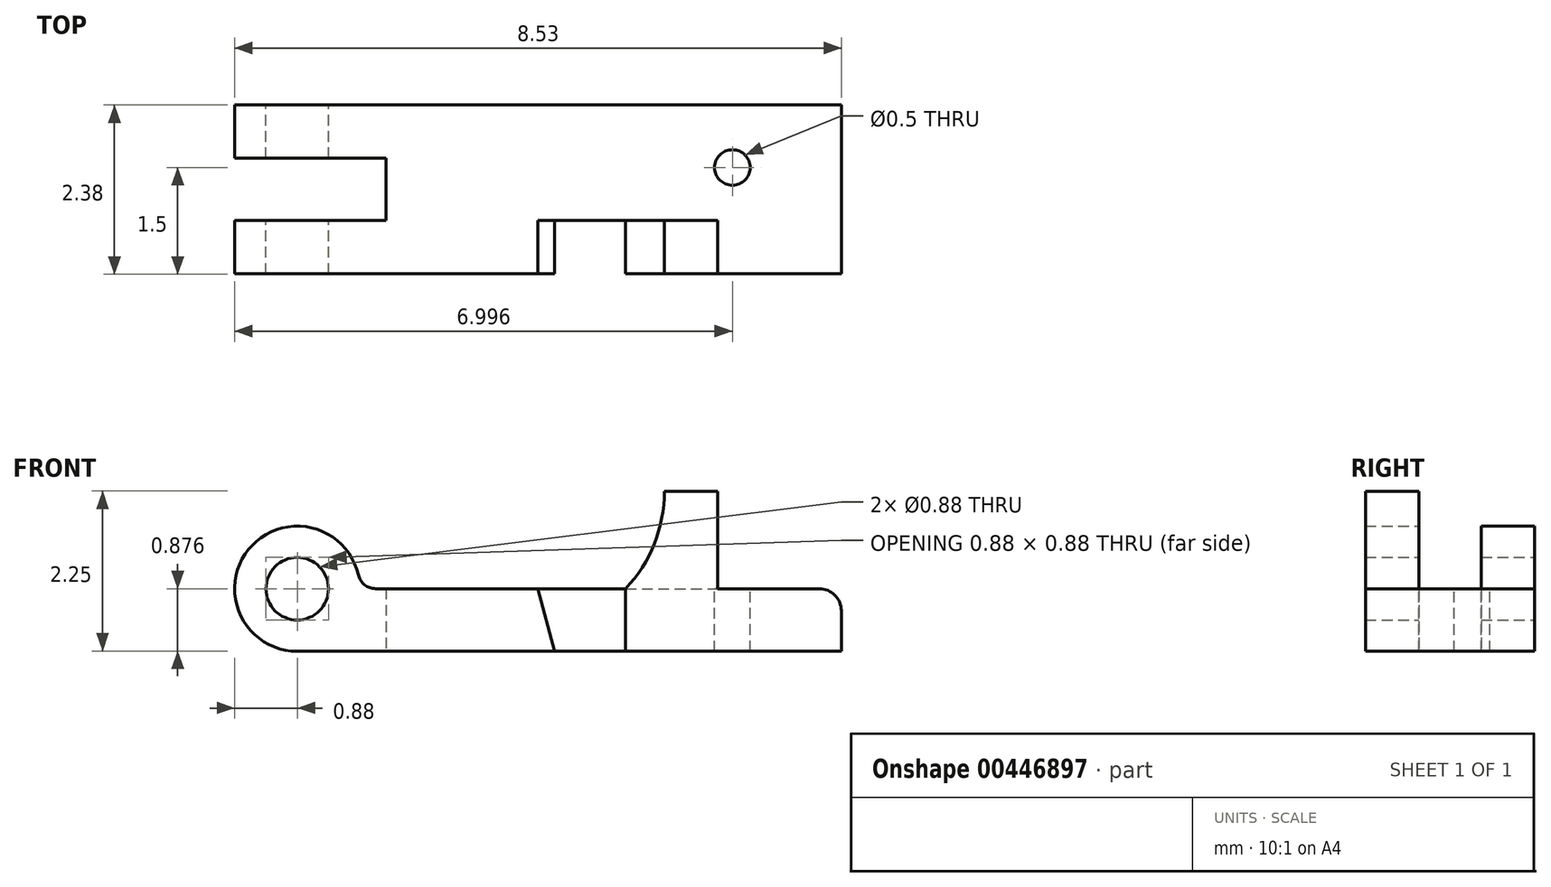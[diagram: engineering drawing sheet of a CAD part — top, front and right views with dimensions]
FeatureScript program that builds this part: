
annotation { "Feature Type Name" : "Feature", "Feature Type Description" : "" }
export const myFeature = defineFeature(function(context is Context, id is Id, definition is map)
    precondition{}
    {
        {
            var Q0;
            Q0=qCreatedBy(makeId("Front.planeOp"),FACE);
            var sketch = newSketch(context, id + "F0", { "sketchPlane" : qUnion([Q0])});
            skArc(sketch, "E0", {"start": v(-5.16, 10.86) * mm, "mid": v(-6.7, 11.22) * mm, "end": v(-6.02, 9.79) * mm});
            skLineSegment(sketch, "E1.bottom", {"start": v(-4.92, 10.67) * mm, "end": v(1.63, 10.67) * mm});
            skLineSegment(sketch, "E1.top", {"start": v(-5.56, 9.79) * mm, "end": v(1.63, 9.79) * mm});
            skLineSegment(sketch, "E1.right", {"start": v(1.63, 10.67) * mm, "end": v(1.63, 9.79) * mm});
            skLineSegment(sketch, "E2", {"start": v(-5.56, 9.79) * mm, "end": v(-6.02, 9.79) * mm});
            skPoint(sketch, "E3.visualSharp", {"position": v(-5.14, 10.67) * mm});
            skArc(sketch, "E3.filletArc", {"start": v(-5.16, 10.86) * mm, "mid": v(-5.07, 10.72) * mm, "end": v(-4.92, 10.67) * mm});
            skCircle(sketch, "E4", {"center": v(-6.02, 10.67) * mm, "radius": 0.44 * mm});
            skSolve(sketch);
        }
        {
            var Q0;
            Q0=makeQuery(id+"F0.imprint","IMPRINT",FACE,{"disambiguationData":[TD([[makeQuery(id+"F0.imprint","IMPRINT",EDGE,{"derivedFrom":sQuery(id+"F0.wireOp",EDGE,"E0")}),1.0]])]});
            extrude(context, id + "F1", {"entities" : qUnion([Q0]), "depth" : 2.38 * mm});
        }
        {
            var Q0;
            Q0=qCreatedBy(makeId("Top.planeOp"),FACE);
            var sketch = newSketch(context, id + "F2", { "sketchPlane" : qUnion([Q0])});
            skLineSegment(sketch, "E5.bottom", {"start": v(-7.37, -0.75) * mm, "end": v(-4.77, -0.75) * mm});
            skLineSegment(sketch, "E5.top", {"start": v(-7.37, -1.63) * mm, "end": v(-4.77, -1.63) * mm});
            skLineSegment(sketch, "E5.left", {"start": v(-7.37, -0.75) * mm, "end": v(-7.37, -1.63) * mm});
            skLineSegment(sketch, "E5.right", {"start": v(-4.77, -0.75) * mm, "end": v(-4.77, -1.63) * mm});
            skSolve(sketch);
        }
        {
            var Q0;
            Q0=makeQuery(id+"F2.imprint","IMPRINT",FACE,{"disambiguationData":[TD([[makeQuery(id+"F2.imprint","IMPRINT",EDGE,{"derivedFrom":sQuery(id+"F2.wireOp",EDGE,"E5.bottom")}),-1.0]])]});
            extrude(context, id + "F3", {"entities" : qUnion([Q0]), "operationType" : NewBodyOperationType.REMOVE, "depth" : 25 * mm});
        }
        {
            var Q0;
            Q0=makeQuery(id+"F1.opExtrude","CAP_FACE",FACE,{"disambiguationData":[OSD([sQuery(id+"F0.wireOp",EDGE,"E0"),sQuery(id+"F0.wireOp",EDGE,"E1.bottom"),sQuery(id+"F0.wireOp",EDGE,"E1.top"),sQuery(id+"F0.wireOp",EDGE,"E1.right"),sQuery(id+"F0.wireOp",EDGE,"E2"),sQuery(id+"F0.wireOp",EDGE,"E3.filletArc"),sQuery(id+"F0.wireOp",EDGE,"E4")])],"isStart":false});
            var sketch = newSketch(context, id + "F4", { "sketchPlane" : qUnion([Q0])});
            skLineSegment(sketch, "E6", {"start": v(-2.64, 10.67) * mm, "end": v(-2.4, 9.79) * mm});
            skLineSegment(sketch, "E7", {"start": v(-1.4, 10.67) * mm, "end": v(-1.4, 9.79) * mm});
            skLineSegment(sketch, "E8.0", {"start": v(-4.92, 10.67) * mm, "end": v(1.63, 10.67) * mm});
            skLineSegment(sketch, "E9.0", {"start": v(1.63, 9.79) * mm, "end": v(-6.02, 9.79) * mm});
            skLineSegment(sketch, "E10.0.0", {"start": v(1.63, 9.79) * mm, "end": v(1.63, 10.67) * mm});
            skLineSegment(sketch, "E10.0.1", {"start": v(1.63, 10.67) * mm, "end": v(-4.92, 10.67) * mm});
            skArc(sketch, "E10.0.2", {"start": v(-4.92, 10.67) * mm, "mid": v(-5.07, 10.72) * mm, "end": v(-5.16, 10.86) * mm});
            skArc(sketch, "E10.0.3", {"start": v(-5.16, 10.86) * mm, "mid": v(-6.7, 11.22) * mm, "end": v(-6.02, 9.79) * mm});
            skLineSegment(sketch, "E10.0.4", {"start": v(-6.02, 9.79) * mm, "end": v(1.63, 9.79) * mm});
            skSolve(sketch);
        }
        {
            var Q0;
            {var subQ0=sQuery(id+"F4.wireOp",EDGE,"E6");Q0=makeQuery(id+"F4.imprint","IMPRINT",FACE,{"disambiguationData":[TD([[makeQuery(id+"F4.imprint","IMPRINT",EDGE,{"derivedFrom":subQ0}),1.0]])]});}
            extrude(context, id + "F5", {"entities" : qUnion([Q0]), "operationType" : NewBodyOperationType.REMOVE, "oppositeDirection" : true, "depth" : 0.75 * mm});
        }
        {
            var Q0;
            {var subQ0=sQuery(id+"F0.wireOp",EDGE,"E1.bottom");var subQ1=sQuery(id+"F0.wireOp",EDGE,"E2");var subQ2=sQuery(id+"F0.wireOp",EDGE,"E1.top");var subQ3=sQuery(id+"F0.wireOp",EDGE,"E1.right");Q0=makeQuery(id+"F5.boolean.opBoolean","SPLIT",FACE,{"disambiguationData":[TD([makeQuery(id+"F1.opExtrude","SWEPT_FACE",FACE,{"disambiguationData":[OSD([subQ3])]})])],"derivedFrom":makeQuery(id+"F1.opExtrude","CAP_FACE",FACE,{"disambiguationData":[OSD([sQuery(id+"F0.wireOp",EDGE,"E0"),subQ0,subQ2,subQ3,subQ1,sQuery(id+"F0.wireOp",EDGE,"E3.filletArc"),sQuery(id+"F0.wireOp",EDGE,"E4")])],"isStart":false})});}
            var sketch = newSketch(context, id + "F6", { "sketchPlane" : qUnion([Q0])});
            skLineSegment(sketch, "E11.0", {"start": v(-1.4, 10.67) * mm, "end": v(-1.4, 9.79) * mm});
            skLineSegment(sketch, "E12", {"start": v(-0.11, 10.67) * mm, "end": v(-0.11, 12.04) * mm});
            skLineSegment(sketch, "E13", {"start": v(-0.11, 12.04) * mm, "end": v(-0.86, 12.04) * mm});
            skArc(sketch, "E14", {"start": v(-1.4, 10.67) * mm, "mid": v(-1, 11.3) * mm, "end": v(-0.86, 12.04) * mm});
            skSolve(sketch);
        }
        {
            var Q0;
            {var subQ0=sQuery(id+"F6.wireOp",EDGE,"E12");Q0=makeQuery(id+"F6.imprint","IMPRINT",FACE,{"disambiguationData":[TD([[makeQuery(id+"F6.imprint","IMPRINT",EDGE,{"derivedFrom":subQ0}),1.0]])]});}
            extrude(context, id + "F7", {"entities" : qUnion([Q0]), "operationType" : NewBodyOperationType.ADD, "oppositeDirection" : true, "depth" : 0.75 * mm});
        }
        {
            var Q0;
            Q0=makeQuery(id+"F1.opExtrude","SWEPT_FACE",FACE,{"disambiguationData":[OSD([sQuery(id+"F0.wireOp",EDGE,"E1.bottom")])]});
            var sketch = newSketch(context, id + "F8", { "sketchPlane" : qUnion([Q0])});
            skCircle(sketch, "E15", {"center": v(0.1, -0.88) * mm, "radius": 0.25 * mm});
            skSolve(sketch);
        }
        {
            var Q0;
            Q0=makeQuery(id+"F8.imprint","IMPRINT",FACE,{"disambiguationData":[TD([[makeQuery(id+"F8.imprint","IMPRINT",EDGE,{"derivedFrom":sQuery(id+"F8.wireOp",EDGE,"E15")}),1.0]])]});
            extrude(context, id + "F9", {"entities" : qUnion([Q0]), "operationType" : NewBodyOperationType.REMOVE, "oppositeDirection" : true, "depth" : 25 * mm});
        }
        {
            var Q0;
            Q0=makeQuery(id+"F1.opExtrude","SWEPT_EDGE",EDGE,{"disambiguationData":[OSD([sQuery(id+"F0.wireOp",EDGE,"E1.bottom"),sQuery(id+"F0.wireOp",EDGE,"E1.right")])]});
            fillet(context, id + "F10", {"entities" : qUnion([Q0]), "radius" : 0.31 * mm, "tangentPropagation" : true, "allowEdgeOverflow" : false});
        }
    });
